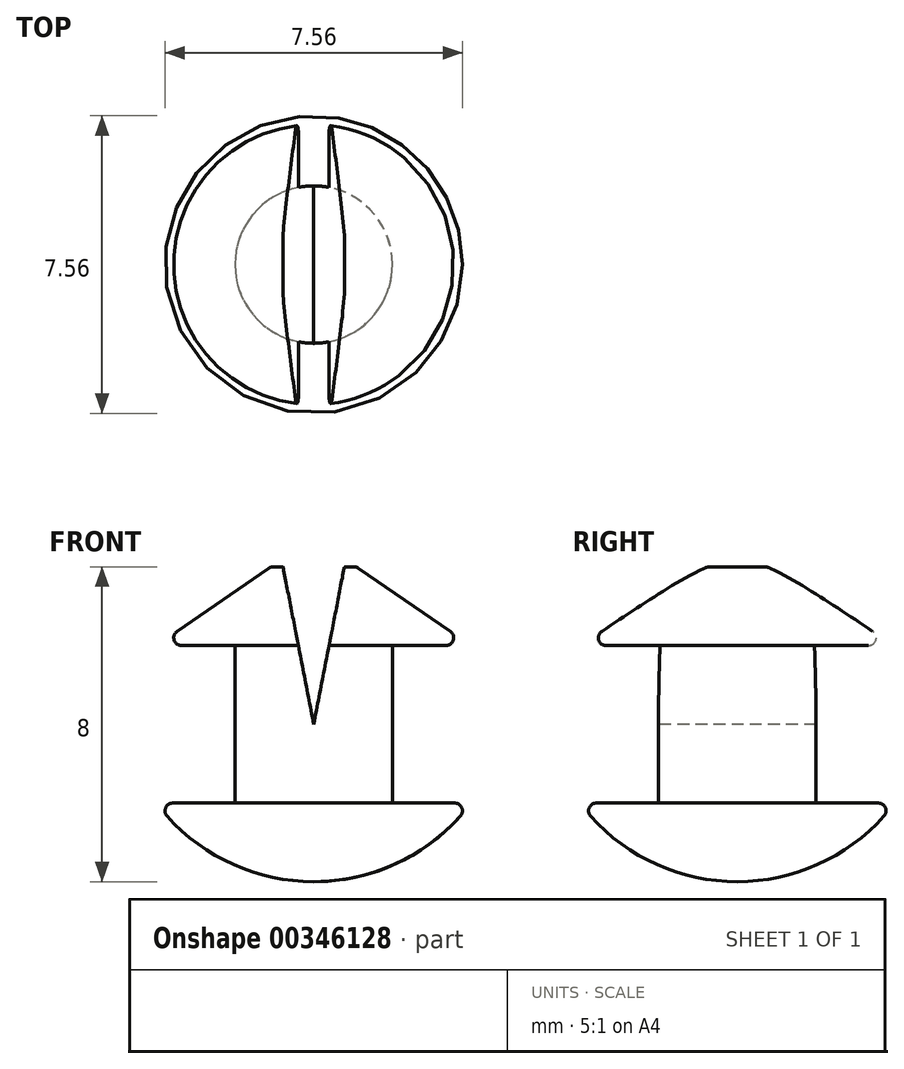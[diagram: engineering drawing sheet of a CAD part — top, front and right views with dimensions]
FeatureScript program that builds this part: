
annotation { "Feature Type Name" : "Feature", "Feature Type Description" : "" }
export const myFeature = defineFeature(function(context is Context, id is Id, definition is map)
    precondition{}
    {
        {
            var Q0;
            Q0=qCreatedBy(makeId("Front.planeOp"),FACE);
            var sketch = newSketch(context, id + "F0", { "sketchPlane" : qUnion([Q0])});
            skLineSegment(sketch, "E0", {"start": v(0, 4) * mm, "end": v(1.1, 4) * mm});
            skLineSegment(sketch, "E1", {"start": v(1.1, 4) * mm, "end": v(4, 2) * mm});
            skLineSegment(sketch, "E2", {"start": v(4, 2) * mm, "end": v(2, 2) * mm});
            skLineSegment(sketch, "E3", {"start": v(2, 2) * mm, "end": v(2, -2) * mm});
            skLineSegment(sketch, "E4", {"start": v(2, -2) * mm, "end": v(4, -2) * mm});
            skArc(sketch, "E5", {"start": v(0, -4) * mm, "mid": v(2.24, -3.47) * mm, "end": v(4, -2) * mm});
            skLineSegment(sketch, "E6", {"start": v(0, 4) * mm, "end": v(0, -4) * mm});
            skLineSegment(sketch, "E7", {"start": v(0, 0) * mm, "end": v(2, 0) * mm, "construction": true});
            skLineSegment(sketch, "E8", {"start": v(0.78, 4) * mm, "end": v(0, 2.16) * mm});
            skLineSegment(sketch, "E9.bottom", {"start": v(2, 0) * mm, "end": v(4, 0) * mm, "construction": true});
            skLineSegment(sketch, "E9.top", {"start": v(2, 2) * mm, "end": v(4, 2) * mm});
            skLineSegment(sketch, "E9.left", {"start": v(2, 0) * mm, "end": v(2, 2) * mm});
            skLineSegment(sketch, "E9.right", {"start": v(4, 0) * mm, "end": v(4, 2) * mm, "construction": true});
            skLineSegment(sketch, "E10.bottom", {"start": v(2, -2) * mm, "end": v(0, -2) * mm, "construction": true});
            skLineSegment(sketch, "E10.top", {"start": v(2, -4) * mm, "end": v(0, -4) * mm, "construction": true});
            skLineSegment(sketch, "E10.left", {"start": v(2, -2) * mm, "end": v(2, -4) * mm, "construction": true});
            skLineSegment(sketch, "E10.right", {"start": v(0, -2) * mm, "end": v(0, -4) * mm, "construction": true});
            skLineSegment(sketch, "E11.bottom", {"start": v(2, 2) * mm, "end": v(0, 2) * mm, "construction": true});
            skLineSegment(sketch, "E11.top", {"start": v(2, 4) * mm, "end": v(0, 4) * mm, "construction": true});
            skLineSegment(sketch, "E11.left", {"start": v(2, 2) * mm, "end": v(2, 4) * mm, "construction": true});
            skLineSegment(sketch, "E11.right", {"start": v(0, 2) * mm, "end": v(0, 4) * mm, "construction": true});
            skSolve(sketch);
        }
        {
            var Q0;
            {var subQ0=sQuery(id+"F0.wireOp",EDGE,"E1");Q0=makeQuery(id+"F0.imprint","IMPRINT",FACE,{"disambiguationData":[TD([[makeQuery(id+"F0.imprint","IMPRINT",EDGE,{"derivedFrom":subQ0}),-1.0]])]});}
            var Q1;
            Q1=sQuery(id+"F0.wireOp",EDGE,"E6");
            revolve(context, id + "F1", {"entities" : qUnion([Q0]), "axis" : qUnion([Q1]), "revolveType" : RevolveType.FULL});
        }
        {
            var Q0;
            Q0=qCreatedBy(makeId("Front.planeOp"),FACE);
            var sketch = newSketch(context, id + "F2", { "sketchPlane" : qUnion([Q0])});
            skLineSegment(sketch, "E12.0", {"start": v(-0.78, 4) * mm, "end": v(0.78, 4) * mm});
            skLineSegment(sketch, "E13", {"start": v(0.78, 4) * mm, "end": v(0, 0) * mm});
            skLineSegment(sketch, "E14", {"start": v(0, 0) * mm, "end": v(-0.78, 4) * mm});
            skSolve(sketch);
        }
        {
            var Q0;
            Q0 = qSketchRegion(id + "F2", true);
            extrude(context, id + "F3", {"entities" : qUnion([Q0]), "operationType" : NewBodyOperationType.REMOVE, "endBound" : BoundingType.SYMMETRIC, "oppositeDirection" : true, "depth" : 25 * mm});
        }
        {
            var Q0;
            {var subQ0=sQuery(id+"F0.wireOp",EDGE,"E1");var subQ1=sQuery(id+"F0.wireOp",EDGE,"E9.top");Q0=makeQuery(id+"F3.boolean.opBoolean","SPLIT",EDGE,{"disambiguationData":[TD([makeQuery(id+"F3.opExtrude","SWEPT_FACE",FACE,{"disambiguationData":[OSD([sQuery(id+"F2.wireOp",EDGE,"E13")])]})])],"derivedFrom":makeQuery(id+"F1.opRevolve","SWEPT_EDGE",EDGE,{"disambiguationData":[OSD([subQ0,subQ1])]})});}
            var Q1;
            {var subQ0=sQuery(id+"F0.wireOp",EDGE,"E1");var subQ1=sQuery(id+"F0.wireOp",EDGE,"E9.top");Q1=makeQuery(id+"F3.boolean.opBoolean","SPLIT",EDGE,{"disambiguationData":[TD([makeQuery(id+"F3.opExtrude","SWEPT_FACE",FACE,{"disambiguationData":[OSD([sQuery(id+"F2.wireOp",EDGE,"E14")])]})])],"derivedFrom":makeQuery(id+"F1.opRevolve","SWEPT_EDGE",EDGE,{"disambiguationData":[OSD([subQ0,subQ1])]})});}
            var Q2;
            Q2=makeQuery(id+"F1.opRevolve","SWEPT_EDGE",EDGE,{"disambiguationData":[OSD([sQuery(id+"F0.wireOp",EDGE,"E4"),sQuery(id+"F0.wireOp",EDGE,"E5")])]});
            fillet(context, id + "F4", {"entities" : qUnion([Q0, Q1, Q2]), "radius" : 0.2 * mm, "tangentPropagation" : true, "allowEdgeOverflow" : false});
        }
        {
            var Q0;
            Q0=makeQuery(id+"F1.opRevolve","SWEPT_BODY",BODY,{"disambiguationData":[OSD([sQuery(id+"F0.wireOp",EDGE,"E0"),sQuery(id+"F0.wireOp",EDGE,"E1"),sQuery(id+"F0.wireOp",EDGE,"E3"),sQuery(id+"F0.wireOp",EDGE,"E4"),sQuery(id+"F0.wireOp",EDGE,"E5"),sQuery(id+"F0.wireOp",EDGE,"E6"),sQuery(id+"F0.wireOp",EDGE,"E8"),sQuery(id+"F0.wireOp",EDGE,"E9.top"),sQuery(id+"F0.wireOp",EDGE,"E9.left")])]});
            transform(context, id + "F5", {"entities" : qUnion([Q0]), "transformType" : TransformType.TRANSLATION_3D, "dx" : -19.8 * mm, "dy" : 0 * mm, "dz" : -17.8 * mm, "makeCopy" : true});
        }
        {
            var Q0;
            Q0=makeQuery(id+"F5.opPattern","COPY",BODY,{"derivedFrom":makeQuery(id+"F1.opRevolve","SWEPT_BODY",BODY,{"disambiguationData":[OSD([sQuery(id+"F0.wireOp",EDGE,"E0"),sQuery(id+"F0.wireOp",EDGE,"E1"),sQuery(id+"F0.wireOp",EDGE,"E3"),sQuery(id+"F0.wireOp",EDGE,"E4"),sQuery(id+"F0.wireOp",EDGE,"E5"),sQuery(id+"F0.wireOp",EDGE,"E6"),sQuery(id+"F0.wireOp",EDGE,"E8"),sQuery(id+"F0.wireOp",EDGE,"E9.top"),sQuery(id+"F0.wireOp",EDGE,"E9.left")])]}),"instanceName":"1"});
            deleteBodies(context, id + "F6", {"entities" : qUnion([Q0])});
        }
    });
